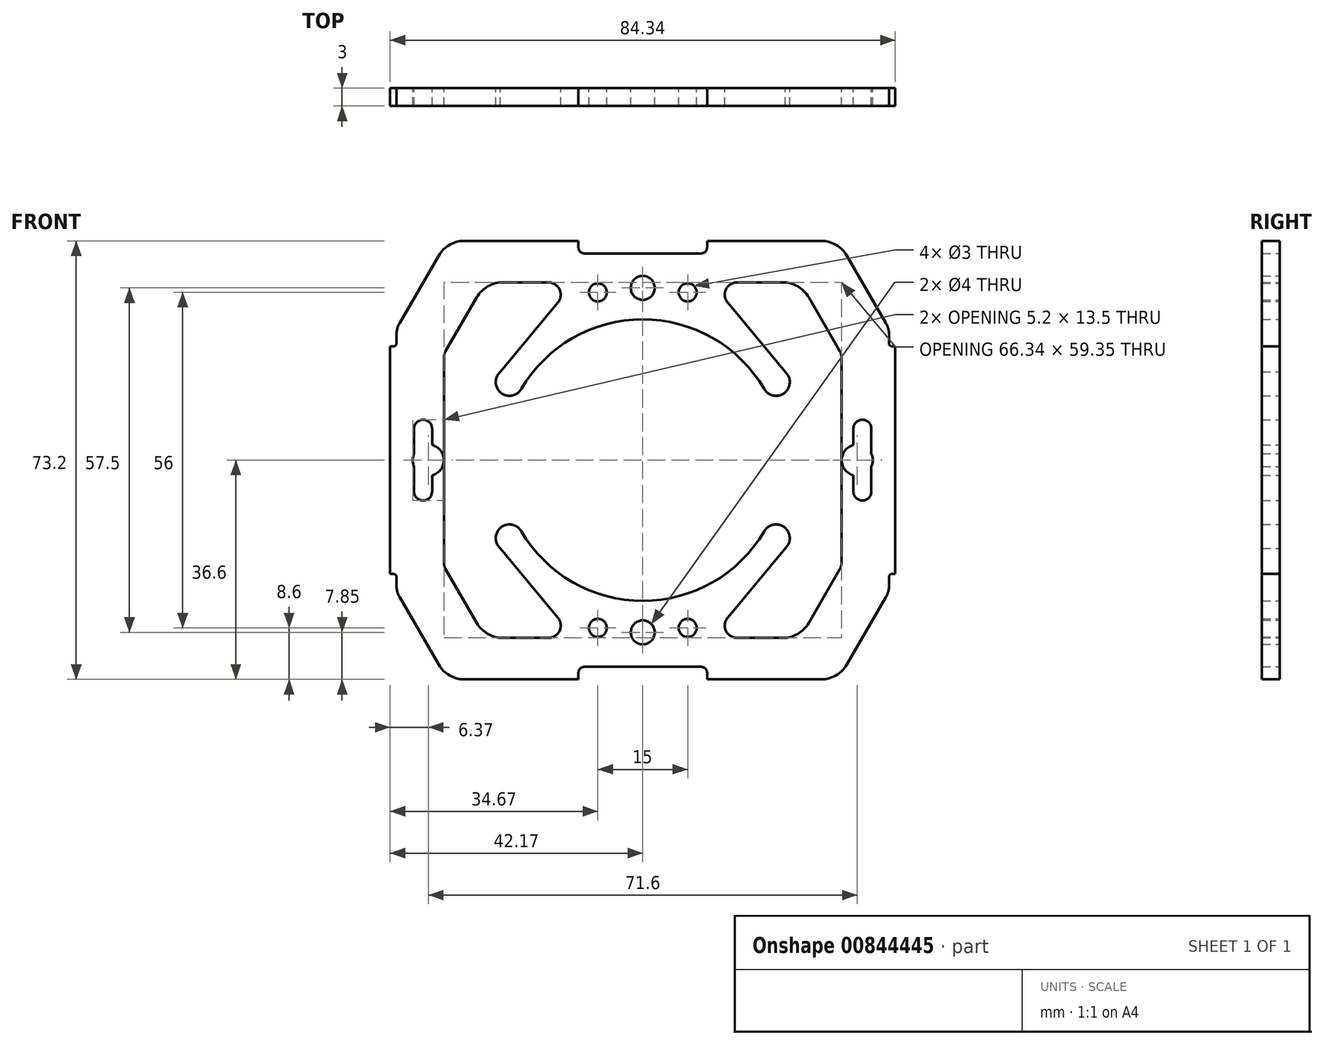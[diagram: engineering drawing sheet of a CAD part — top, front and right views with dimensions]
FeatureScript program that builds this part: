
annotation { "Feature Type Name" : "Feature", "Feature Type Description" : "" }
export const myFeature = defineFeature(function(context is Context, id is Id, definition is map)
    precondition{}
    {
        {
            var Q0;
            Q0=qCreatedBy(makeId("Front.planeOp"),FACE);
            var sketch = newSketch(context, id + "F0", { "sketchPlane" : qUnion([Q0])});
            skCircle(sketch, "E0", {"center": v(0, 28.75) * mm, "radius": 2 * mm});
            skCircle(sketch, "E1.MirrorC", {"center": v(7.5, 28) * mm, "radius": 1.5 * mm});
            skLineSegment(sketch, "E2", {"start": v(41.11, 20.92) * mm, "end": v(41.11, 19.5) * mm});
            skLineSegment(sketch, "E3", {"start": v(41.61, 19) * mm, "end": v(42.17, 19) * mm});
            skPoint(sketch, "E4.visualSharp", {"position": v(41.11, 19) * mm});
            skArc(sketch, "E4.filletArc", {"start": v(41.11, 19.5) * mm, "mid": v(41.26, 19.15) * mm, "end": v(41.61, 19) * mm});
            skArc(sketch, "E5.MirrorCS", {"start": v(40.57, 22.93) * mm, "mid": v(40.97, 21.96) * mm, "end": v(41.11, 20.92) * mm});
            skPoint(sketch, "E6.MirrorP", {"position": v(41.11, 22) * mm});
            skLineSegment(sketch, "E7.MirrorCS", {"start": v(34.08, 34.11) * mm, "end": v(40.57, 22.93) * mm});
            skLineSegment(sketch, "E8.0", {"start": v(27.7, 27.18) * mm, "end": v(32.9, 18.23) * mm});
            skPoint(sketch, "E9.visualSharp", {"position": v(26.25, 29.67) * mm});
            skArc(sketch, "E9.filletArc", {"start": v(27.7, 27.18) * mm, "mid": v(25.86, 29) * mm, "end": v(23.37, 29.67) * mm});
            skLineSegment(sketch, "E10", {"start": v(23.77, 14.75) * mm, "end": v(14.18, 26.28) * mm});
            skArc(sketch, "E11", {"start": v(20.28, 11.88) * mm, "mid": v(23.7, 11.27) * mm, "end": v(23.77, 14.75) * mm});
            skPoint(sketch, "E12.visualSharp", {"position": v(11.35, 29.67) * mm});
            skArc(sketch, "E12.filletArc", {"start": v(15.77, 29.67) * mm, "mid": v(13.9, 28.48) * mm, "end": v(14.18, 26.28) * mm});
            skArc(sketch, "E13.MirrorC", {"start": v(38.17, 1.07) * mm, "mid": v(38.34, 0.55) * mm, "end": v(38.4, 0) * mm});
            skLineSegment(sketch, "E14", {"start": v(42.17, 19) * mm, "end": v(42.17, 0) * mm});
            skPoint(sketch, "E15.visualSharp", {"position": v(33.17, 17.75) * mm});
            skArc(sketch, "E15.filletArc", {"start": v(33.17, 17.2) * mm, "mid": v(33.1, 17.73) * mm, "end": v(32.9, 18.23) * mm});
            skLineSegment(sketch, "E16.0", {"start": v(35.17, 5.25) * mm, "end": v(35.17, 2.52) * mm});
            skLineSegment(sketch, "E17.0", {"start": v(38.17, 5.25) * mm, "end": v(38.17, 1.07) * mm});
            skArc(sketch, "E18", {"start": v(38.17, 5.25) * mm, "mid": v(36.67, 6.75) * mm, "end": v(35.17, 5.25) * mm});
            skArc(sketch, "E19.trimOffspring", {"start": v(33.2, 0) * mm, "mid": v(33.75, 1.6) * mm, "end": v(35.17, 2.52) * mm});
            skPoint(sketch, "E20.visualSharp", {"position": v(32.63, 36.6) * mm});
            skArc(sketch, "E20.filletArc", {"start": v(34.08, 34.11) * mm, "mid": v(32.25, 35.93) * mm, "end": v(29.75, 36.6) * mm});
            skLineSegment(sketch, "E21", {"start": v(33.17, 17.2) * mm, "end": v(33.17, 0) * mm});
            skLineSegment(sketch, "E22", {"start": v(33.17, 0) * mm, "end": v(33.2, 0) * mm});
            skPoint(sketch, "E23.MirrorCS.end.orphan", {"position": v(42.17, 0) * mm});
            skLineSegment(sketch, "E24.MirrorCS", {"start": v(9.74, 34.5) * mm, "end": v(0, 34.5) * mm});
            skArc(sketch, "E25.MirrorCS", {"start": v(10.74, 35.5) * mm, "mid": v(10.45, 34.8) * mm, "end": v(9.74, 34.5) * mm});
            skLineSegment(sketch, "E26.MirrorCS", {"start": v(10.74, 35.5) * mm, "end": v(10.74, 36.6) * mm});
            skLineSegment(sketch, "E27.MirrorCS", {"start": v(29.75, 36.6) * mm, "end": v(10.74, 36.6) * mm});
            skArc(sketch, "E28", {"start": v(20.28, 11.88) * mm, "mid": v(11.69, 20.39) * mm, "end": v(0, 23.5) * mm});
            skLineSegment(sketch, "E29.MirrorCS", {"start": v(-41.11, 20.92) * mm, "end": v(-41.11, 19.5) * mm});
            skArc(sketch, "E30.MirrorCS", {"start": v(-41.11, 19.5) * mm, "mid": v(-41.26, 19.15) * mm, "end": v(-41.61, 19) * mm});
            skLineSegment(sketch, "E31.MirrorCS", {"start": v(-41.61, 19) * mm, "end": v(-42.17, 19) * mm});
            skLineSegment(sketch, "E32.MirrorCS", {"start": v(-33.17, 0) * mm, "end": v(-33.2, 0) * mm});
            skArc(sketch, "E33.MirrorCS", {"start": v(-33.17, 17.2) * mm, "mid": v(-33.1, 17.73) * mm, "end": v(-32.9, 18.23) * mm});
            skLineSegment(sketch, "E34.MirrorCS", {"start": v(-35.17, 5.25) * mm, "end": v(-35.17, 2.52) * mm});
            skArc(sketch, "E35.MirrorCS", {"start": v(-38.17, 1.07) * mm, "mid": v(-38.34, 0.55) * mm, "end": v(-38.4, 0) * mm});
            skArc(sketch, "E36.MirrorCS", {"start": v(-40.57, 22.93) * mm, "mid": v(-40.97, 21.96) * mm, "end": v(-41.11, 20.92) * mm});
            skLineSegment(sketch, "E37.MirrorCS", {"start": v(-10.74, 35.5) * mm, "end": v(-10.74, 36.6) * mm});
            skArc(sketch, "E38.MirrorCS", {"start": v(-10.74, 35.5) * mm, "mid": v(-10.45, 34.8) * mm, "end": v(-9.74, 34.5) * mm});
            skArc(sketch, "E39.MirrorCS", {"start": v(-34.08, 34.11) * mm, "mid": v(-32.25, 35.93) * mm, "end": v(-29.75, 36.6) * mm});
            skArc(sketch, "E40.MirrorCS", {"start": v(-27.7, 27.18) * mm, "mid": v(-25.86, 29) * mm, "end": v(-23.37, 29.67) * mm});
            skPoint(sketch, "E41.MirrorP", {"position": v(-41.11, 22) * mm});
            skLineSegment(sketch, "E42.MirrorCS", {"start": v(-23.77, 14.75) * mm, "end": v(-14.18, 26.28) * mm});
            skArc(sketch, "E43.MirrorCS", {"start": v(-38.17, 5.25) * mm, "mid": v(-36.67, 6.75) * mm, "end": v(-35.17, 5.25) * mm});
            skPoint(sketch, "E44.MirrorP", {"position": v(-32.63, 36.6) * mm});
            skPoint(sketch, "E45.MirrorP", {"position": v(-11.35, 29.67) * mm});
            skArc(sketch, "E46.MirrorCS", {"start": v(-20.28, 11.88) * mm, "mid": v(-11.69, 20.39) * mm, "end": v(0, 23.5) * mm});
            skLineSegment(sketch, "E47.MirrorCS", {"start": v(-29.75, 36.6) * mm, "end": v(-10.74, 36.6) * mm});
            skLineSegment(sketch, "E48.MirrorCS", {"start": v(-34.08, 34.11) * mm, "end": v(-40.57, 22.93) * mm});
            skLineSegment(sketch, "E49.MirrorCS", {"start": v(-38.17, 5.25) * mm, "end": v(-38.17, 1.07) * mm});
            skLineSegment(sketch, "E50.MirrorCS", {"start": v(-9.74, 34.5) * mm, "end": v(0, 34.5) * mm});
            skPoint(sketch, "E51.MirrorP", {"position": v(-42.17, 0) * mm});
            skPoint(sketch, "E52.MirrorP", {"position": v(-33.17, 17.75) * mm});
            skCircle(sketch, "E53.MirrorC", {"center": v(-7.5, 28) * mm, "radius": 1.5 * mm});
            skPoint(sketch, "E54.MirrorP", {"position": v(-41.11, 19) * mm});
            skLineSegment(sketch, "E55.MirrorCS", {"start": v(-42.17, 19) * mm, "end": v(-42.17, 0) * mm});
            skArc(sketch, "E56.MirrorCS", {"start": v(-15.77, 29.67) * mm, "mid": v(-13.9, 28.48) * mm, "end": v(-14.18, 26.28) * mm});
            skArc(sketch, "E57.MirrorCS", {"start": v(-33.2, 0) * mm, "mid": v(-33.75, 1.6) * mm, "end": v(-35.17, 2.52) * mm});
            skLineSegment(sketch, "E58.MirrorCS", {"start": v(-27.7, 27.18) * mm, "end": v(-32.9, 18.23) * mm});
            skLineSegment(sketch, "E59.MirrorCS", {"start": v(-33.17, 17.2) * mm, "end": v(-33.17, 0) * mm});
            skPoint(sketch, "E60.MirrorP", {"position": v(-26.25, 29.67) * mm});
            skArc(sketch, "E61.MirrorCS", {"start": v(-20.28, 11.88) * mm, "mid": v(-23.7, 11.27) * mm, "end": v(-23.77, 14.75) * mm});
            skArc(sketch, "E62.MirrorCS", {"start": v(41.11, -19.5) * mm, "mid": v(41.26, -19.15) * mm, "end": v(41.61, -19) * mm});
            skArc(sketch, "E63.MirrorCS", {"start": v(-41.11, -19.5) * mm, "mid": v(-41.26, -19.15) * mm, "end": v(-41.61, -19) * mm});
            skLineSegment(sketch, "E64.MirrorCS", {"start": v(-41.11, -20.92) * mm, "end": v(-41.11, -19.5) * mm});
            skLineSegment(sketch, "E65.MirrorCS", {"start": v(41.11, -20.92) * mm, "end": v(41.11, -19.5) * mm});
            skLineSegment(sketch, "E66.MirrorCS", {"start": v(-41.61, -19) * mm, "end": v(-42.17, -19) * mm});
            skLineSegment(sketch, "E67.MirrorCS", {"start": v(41.61, -19) * mm, "end": v(42.17, -19) * mm});
            skArc(sketch, "E68.MirrorCS", {"start": v(-10.74, -35.5) * mm, "mid": v(-10.45, -34.8) * mm, "end": v(-9.74, -34.5) * mm});
            skLineSegment(sketch, "E69.MirrorCS", {"start": v(-10.74, -35.5) * mm, "end": v(-10.74, -36.6) * mm});
            skArc(sketch, "E70.MirrorCS", {"start": v(-40.57, -22.93) * mm, "mid": v(-40.97, -21.96) * mm, "end": v(-41.11, -20.92) * mm});
            skArc(sketch, "E71.MirrorCS", {"start": v(40.57, -22.93) * mm, "mid": v(40.97, -21.96) * mm, "end": v(41.11, -20.92) * mm});
            skArc(sketch, "E72.MirrorCS", {"start": v(-33.17, -17.2) * mm, "mid": v(-33.1, -17.73) * mm, "end": v(-32.9, -18.23) * mm});
            skArc(sketch, "E73.MirrorCS", {"start": v(33.17, -17.2) * mm, "mid": v(33.1, -17.73) * mm, "end": v(32.9, -18.23) * mm});
            skLineSegment(sketch, "E74.MirrorCS", {"start": v(-35.17, -5.25) * mm, "end": v(-35.17, -2.52) * mm});
            skArc(sketch, "E75.MirrorCS", {"start": v(-33.2, 0) * mm, "mid": v(-33.75, -1.6) * mm, "end": v(-35.17, -2.52) * mm});
            skArc(sketch, "E76.MirrorCS", {"start": v(33.2, 0) * mm, "mid": v(33.75, -1.6) * mm, "end": v(35.17, -2.52) * mm});
            skArc(sketch, "E77.MirrorCS", {"start": v(-38.17, -1.07) * mm, "mid": v(-38.34, -0.55) * mm, "end": v(-38.4, 0) * mm});
            skArc(sketch, "E78.MirrorCS", {"start": v(-34.08, -34.11) * mm, "mid": v(-32.25, -35.93) * mm, "end": v(-29.75, -36.6) * mm});
            skArc(sketch, "E79.MirrorCS", {"start": v(15.77, -29.67) * mm, "mid": v(13.9, -28.48) * mm, "end": v(14.18, -26.28) * mm});
            skArc(sketch, "E80.MirrorCS", {"start": v(10.74, -35.5) * mm, "mid": v(10.45, -34.8) * mm, "end": v(9.74, -34.5) * mm});
            skArc(sketch, "E81.MirrorCS", {"start": v(38.17, -5.25) * mm, "mid": v(36.67, -6.75) * mm, "end": v(35.17, -5.25) * mm});
            skArc(sketch, "E82.MirrorCS", {"start": v(-38.17, -5.25) * mm, "mid": v(-36.67, -6.75) * mm, "end": v(-35.17, -5.25) * mm});
            skArc(sketch, "E83.MirrorCS", {"start": v(38.17, -1.07) * mm, "mid": v(38.34, -0.55) * mm, "end": v(38.4, 0) * mm});
            skLineSegment(sketch, "E84.MirrorCS", {"start": v(10.74, -35.5) * mm, "end": v(10.74, -36.6) * mm});
            skLineSegment(sketch, "E85.MirrorCS", {"start": v(35.17, -5.25) * mm, "end": v(35.17, -2.52) * mm});
            skCircle(sketch, "E86.MirrorC", {"center": v(0, -28.75) * mm, "radius": 2 * mm});
            skPoint(sketch, "E87.MirrorP", {"position": v(-41.11, -22) * mm});
            skArc(sketch, "E88.MirrorCS", {"start": v(-20.28, -11.88) * mm, "mid": v(-11.69, -20.39) * mm, "end": v(0, -23.5) * mm});
            skLineSegment(sketch, "E89.MirrorCS", {"start": v(-23.77, -14.75) * mm, "end": v(-14.18, -26.28) * mm});
            skArc(sketch, "E90.MirrorCS", {"start": v(-20.28, -11.88) * mm, "mid": v(-23.7, -11.27) * mm, "end": v(-23.77, -14.75) * mm});
            skArc(sketch, "E91.MirrorCS", {"start": v(-27.7, -27.18) * mm, "mid": v(-25.86, -29) * mm, "end": v(-23.37, -29.67) * mm});
            skPoint(sketch, "E92.MirrorP", {"position": v(41.11, -22) * mm});
            skArc(sketch, "E93.MirrorCS", {"start": v(34.08, -34.11) * mm, "mid": v(32.25, -35.93) * mm, "end": v(29.75, -36.6) * mm});
            skArc(sketch, "E94.MirrorCS", {"start": v(-15.77, -29.67) * mm, "mid": v(-13.9, -28.48) * mm, "end": v(-14.18, -26.28) * mm});
            skLineSegment(sketch, "E95.MirrorCS", {"start": v(-29.75, -36.6) * mm, "end": v(-10.74, -36.6) * mm});
            skArc(sketch, "E96.MirrorCS", {"start": v(20.28, -11.88) * mm, "mid": v(11.69, -20.39) * mm, "end": v(0, -23.5) * mm});
            skLineSegment(sketch, "E97.MirrorCS", {"start": v(23.77, -14.75) * mm, "end": v(14.18, -26.28) * mm});
            skArc(sketch, "E98.MirrorCS", {"start": v(27.7, -27.18) * mm, "mid": v(25.86, -29) * mm, "end": v(23.37, -29.67) * mm});
            skArc(sketch, "E99.MirrorCS", {"start": v(20.28, -11.88) * mm, "mid": v(23.7, -11.27) * mm, "end": v(23.77, -14.75) * mm});
            skLineSegment(sketch, "E100.MirrorCS", {"start": v(-42.17, -19) * mm, "end": v(-42.17, 0) * mm});
            skPoint(sketch, "E101.MirrorP", {"position": v(-41.11, -19) * mm});
            skPoint(sketch, "E102.MirrorP", {"position": v(-32.63, -36.6) * mm});
            skLineSegment(sketch, "E103.MirrorCS", {"start": v(27.7, -27.18) * mm, "end": v(32.9, -18.23) * mm});
            skPoint(sketch, "E104.MirrorP", {"position": v(11.35, -29.67) * mm});
            skPoint(sketch, "E105.MirrorP", {"position": v(41.11, -19) * mm});
            skLineSegment(sketch, "E106.MirrorCS", {"start": v(-9.74, -34.5) * mm, "end": v(0, -34.5) * mm});
            skCircle(sketch, "E107.MirrorC", {"center": v(-7.5, -28) * mm, "radius": 1.5 * mm});
            skLineSegment(sketch, "E108.MirrorCS", {"start": v(-38.17, -5.25) * mm, "end": v(-38.17, -1.07) * mm});
            skPoint(sketch, "E109.MirrorP", {"position": v(-11.35, -29.67) * mm});
            skPoint(sketch, "E110.MirrorP", {"position": v(-26.25, -29.67) * mm});
            skCircle(sketch, "E111.MirrorC", {"center": v(7.5, -28) * mm, "radius": 1.5 * mm});
            skPoint(sketch, "E112.MirrorP", {"position": v(33.17, -17.75) * mm});
            skLineSegment(sketch, "E113.MirrorCS", {"start": v(42.17, -19) * mm, "end": v(42.17, 0) * mm});
            skLineSegment(sketch, "E114.MirrorCS", {"start": v(38.17, -5.25) * mm, "end": v(38.17, -1.07) * mm});
            skPoint(sketch, "E115.MirrorP", {"position": v(-33.17, -17.75) * mm});
            skPoint(sketch, "E116.MirrorP", {"position": v(32.63, -36.6) * mm});
            skLineSegment(sketch, "E117.MirrorCS", {"start": v(9.74, -34.5) * mm, "end": v(0, -34.5) * mm});
            skLineSegment(sketch, "E118.MirrorCS", {"start": v(34.08, -34.11) * mm, "end": v(40.57, -22.93) * mm});
            skLineSegment(sketch, "E119.MirrorCS", {"start": v(29.75, -36.6) * mm, "end": v(10.74, -36.6) * mm});
            skPoint(sketch, "E120.MirrorP", {"position": v(26.25, -29.67) * mm});
            skLineSegment(sketch, "E121.MirrorCS", {"start": v(-27.7, -27.18) * mm, "end": v(-32.9, -18.23) * mm});
            skLineSegment(sketch, "E122.MirrorCS", {"start": v(33.17, -17.2) * mm, "end": v(33.17, 0) * mm});
            skLineSegment(sketch, "E123.MirrorCS", {"start": v(-34.08, -34.11) * mm, "end": v(-40.57, -22.93) * mm});
            skLineSegment(sketch, "E124.MirrorCS", {"start": v(-33.17, -17.2) * mm, "end": v(-33.17, 0) * mm});
            skLineSegment(sketch, "E125", {"start": v(-23.37, 29.67) * mm, "end": v(-15.77, 29.67) * mm});
            skLineSegment(sketch, "E126", {"start": v(15.77, -29.67) * mm, "end": v(23.37, -29.67) * mm});
            skLineSegment(sketch, "E127", {"start": v(15.77, 29.67) * mm, "end": v(23.37, 29.67) * mm});
            skLineSegment(sketch, "E128", {"start": v(-23.37, -29.67) * mm, "end": v(-15.77, -29.67) * mm});
            skSolve(sketch);
        }
        {
            var Q0;
            Q0 = qSketchRegion(id + "F0", true);
            extrude(context, id + "F1", {"entities" : qUnion([Q0]), "depth" : 3 * mm, "offsetDistance" : 25 * mm});
        }
    });
